# Revit family: Toilet_Seat-Round_Closed_Front-KOHLER-RUTLEDGE_READLATCH-K-78052_1
name_source: partatom
category: Specialty Equipment
revit_build: Autodesk Revit 2017 (Build: 20160225_1515(x64)
units: mm (PartAtom-declared; Revit-internal decimal feet)

## family parameters
Cut with Voids When Loaded = No
Host = Face
OmniClass Number = 23.31.19.19.17
OmniClass Title = Water Closet Seats
Part Type = Normal
Room Calculation Point = No
Round Connector Dimension = Use Diameter
Shared = No

## types (1)
- 0-White
    ADA Compliant = No
    Assembly Code = C1030200
    Date Modified = 09/30/2021
    Default Elevation = 15"
    Description = QUEIT CLOSE ROUND FRONT TOILET SEAT
    Finish = Kohler-Plastic-0-White
    Height = 2 1/4"
    Length = 17 11/16"
    Manufacturer = KOHLER Co.
    Master Format 2014 = 10 28 00
    Master Format 2014 Name = Toilet, Bath, and Laundry Accessories
    Material = Plastic
    Model = K-78052-RL-0
    Product Documentation Link = https://www.us.kohler.com
    Product Name = RUTLEDGE READYLATCH
    Product Page URL = http://www.us.kohler.com
    Type = 1
    URL = https://www.us.kohler.com
    WaterSense Certified = No
    Width = 14 3/16"

## geometry (parser evidence)
native form markers: Sweep x5
no freeform markers — native parametric forms only
